# Revit family: Cleanout_Access_4220S02-04_JRSmith
name_source: partatom
category: Plumbing Fixtures
units: mm (PartAtom-declared; Revit-internal decimal feet)

## family parameters
Always vertical = Yes
Cut with Voids When Loaded = No
Part Type = Normal
Room Calculation Point = No
Round Connector Dimension = Use Radius
Shared = No
Work Plane-Based = Yes

## types (3) — shared parameters
04 CSI = 22 05 76
95 CSI = 15155
Assembly Code = D2030400
Default Elevation = 0"
Description = Duco cast iron cleanout with round adjustable scoriated secured cast iron top
Manufacturer = Jay R. Smith Mfg. Co.
Material = Cast Iron
Material Finish = Duco Coated
Model = 4223
No-Hub Connection = Yes
OmniClass Code = 22-22 05 76
OmniClass Title = Facility Drainage Piping Cleanouts
Product URL = http://www.jrsmith.com
SMARTBIM Object Version = 3
SMARTBIM URL = www.smartbim.com
Technical and Installation = http://www.jrsmith.com
URL = http://www.jrsmith.com
Warranty = 1 year material and workmanship
Weight (lb) = 29.67

## per-type parameters (varying)
| type | Outlet Diameter | Outlet Radius |
| 4220S02 | 2" | 1" |
| 4220S03 | 3" | 1 1/2" |
| 4220S04 | 3" | 1 1/2" |

## geometry (parser evidence)
native form markers: Sweep x6
no freeform markers — native parametric forms only
